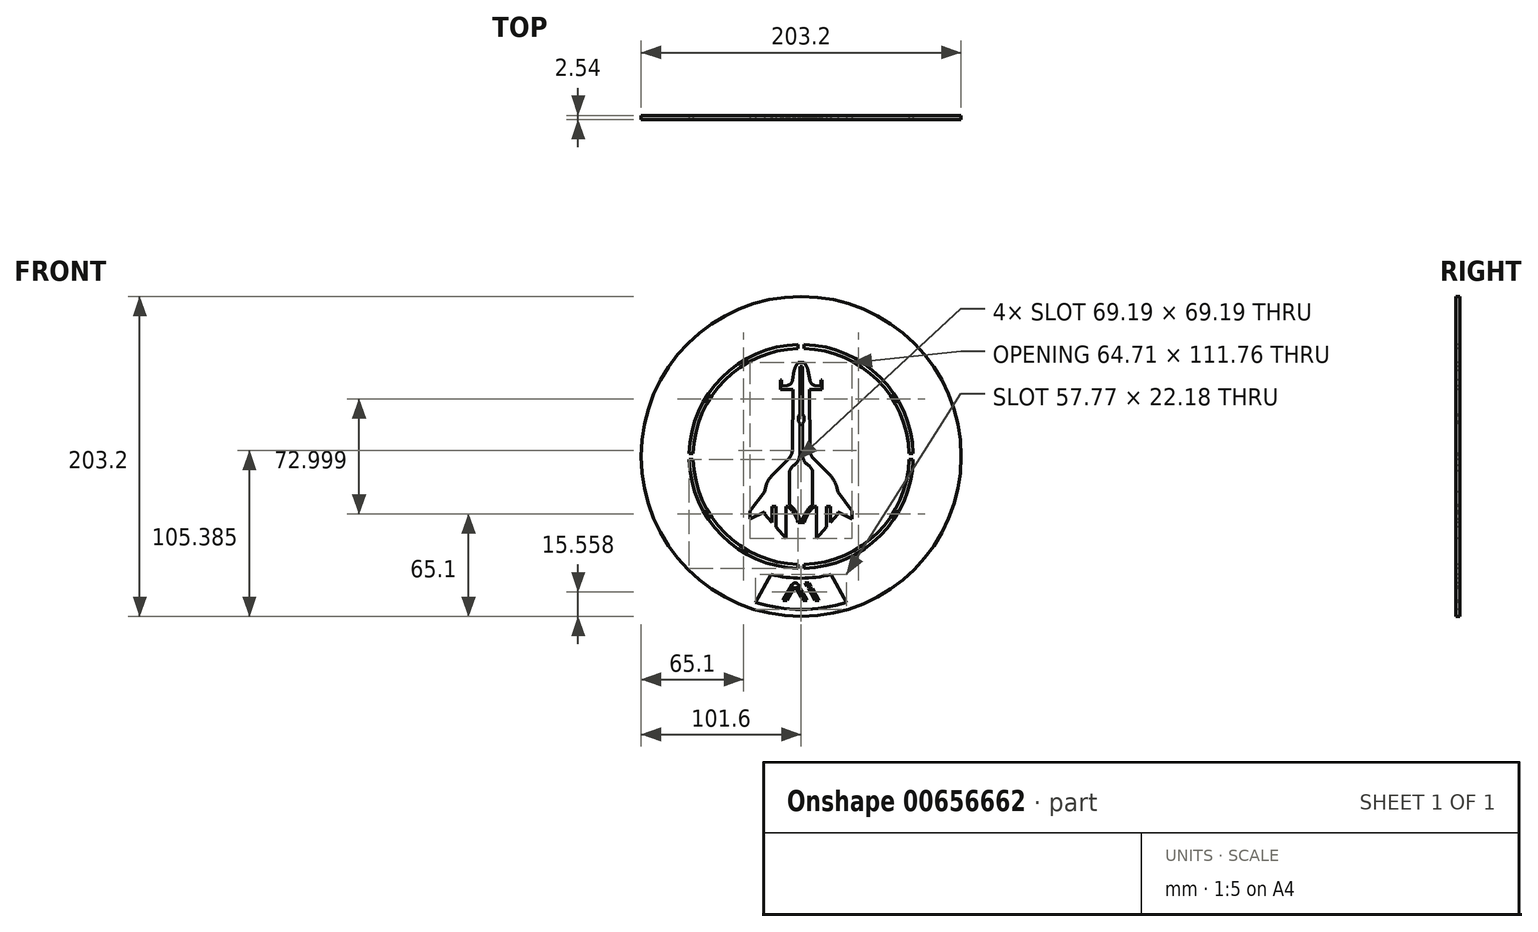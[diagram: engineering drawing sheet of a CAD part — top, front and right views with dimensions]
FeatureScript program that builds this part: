
annotation { "Feature Type Name" : "Feature", "Feature Type Description" : "" }
export const myFeature = defineFeature(function(context is Context, id is Id, definition is map)
    precondition{}
    {
        {
            var Q0;
            Q0=qCreatedBy(makeId("Front.planeOp"),FACE);
            var sketch = newSketch(context, id + "F0", { "sketchPlane" : qUnion([Q0])});
            skCircle(sketch, "E0", {"center": v(0, 0) * mm, "radius": 101.6 * mm});
            skSolve(sketch);
        }
        {
            var Q0;
            Q0=makeQuery(id+"F0.imprint","IMPRINT",FACE,{"disambiguationData":[TD([[makeQuery(id+"F0.imprint","IMPRINT",EDGE,{"derivedFrom":sQuery(id+"F0.wireOp",EDGE,"E0")}),1.0]])]});
            extrude(context, id + "F1", {"entities" : qUnion([Q0]), "oppositeDirection" : true, "depth" : 2.54 * mm, "offsetDistance" : 25.4 * mm});
        }
        {
            var Q0;
            Q0=makeQuery(id+"F1.opExtrude","CAP_FACE",FACE,{"disambiguationData":[OSD([sQuery(id+"F0.wireOp",EDGE,"E0")])],"isStart":true});
            var sketch = newSketch(context, id + "F2", { "sketchPlane" : qUnion([Q0])});
            skArc(sketch, "E1", {"start": v(-71.1, -1.9) * mm, "mid": v(-50.29, -50.29) * mm, "end": v(-1.9, -71.1) * mm});
            skArc(sketch, "E2", {"start": v(-68.55, -1.9) * mm, "mid": v(-48.5, -48.5) * mm, "end": v(-1.9, -68.55) * mm});
            skLineSegment(sketch, "E3", {"start": v(-68.55, 1.9) * mm, "end": v(-71.1, 1.9) * mm});
            skLineSegment(sketch, "E4", {"start": v(-68.55, -1.9) * mm, "end": v(-71.1, -1.9) * mm});
            skLineSegment(sketch, "E5.1.0", {"start": v(-1.9, 68.55) * mm, "end": v(-1.9, 71.1) * mm});
            skLineSegment(sketch, "E5.1.1", {"start": v(1.9, 68.55) * mm, "end": v(1.9, 71.1) * mm});
            skLineSegment(sketch, "E5.2.0", {"start": v(68.55, 1.9) * mm, "end": v(71.1, 1.9) * mm});
            skLineSegment(sketch, "E5.2.1", {"start": v(68.55, -1.9) * mm, "end": v(71.1, -1.9) * mm});
            skLineSegment(sketch, "E5.anchor1", {"start": v(0, 0) * mm, "end": v(-71.1, -1.9) * mm, "construction": true});
            skLineSegment(sketch, "E5.anchor2", {"start": v(0, 0) * mm, "end": v(71.1, 1.9) * mm, "construction": true});
            skLineSegment(sketch, "E6.1.0", {"start": v(1.9, -68.55) * mm, "end": v(1.9, -71.1) * mm});
            skLineSegment(sketch, "E6.1.1", {"start": v(-1.9, -68.55) * mm, "end": v(-1.9, -71.1) * mm});
            skLineSegment(sketch, "E6.anchor1", {"start": v(0, 0) * mm, "end": v(68.55, 1.9) * mm, "construction": true});
            skLineSegment(sketch, "E6.anchor2", {"start": v(0, 0) * mm, "end": v(-68.55, -1.9) * mm, "construction": true});
            skArc(sketch, "E7.trimOffspring", {"start": v(1.9, -68.55) * mm, "mid": v(48.5, -48.5) * mm, "end": v(68.55, -1.9) * mm});
            skArc(sketch, "E8.trimOffspring", {"start": v(1.9, -71.1) * mm, "mid": v(50.29, -50.29) * mm, "end": v(71.1, -1.9) * mm});
            skArc(sketch, "E9.trimOffspring", {"start": v(68.56, 1.84) * mm, "mid": v(48.52, 48.47) * mm, "end": v(1.9, 68.55) * mm});
            skArc(sketch, "E10.trimOffspring", {"start": v(71.1, 1.9) * mm, "mid": v(50.29, 50.29) * mm, "end": v(1.9, 71.1) * mm});
            skArc(sketch, "E11.trimOffspring", {"start": v(-1.9, 68.55) * mm, "mid": v(-48.5, 48.5) * mm, "end": v(-68.55, 1.9) * mm});
            skArc(sketch, "E12.trimOffspring", {"start": v(-1.9, 71.1) * mm, "mid": v(-50.29, 50.29) * mm, "end": v(-71.1, 1.9) * mm});
            skSolve(sketch);
        }
        {
            var Q0;
            Q0 = qSketchRegion(id + "F2", true);
            extrude(context, id + "F3", {"entities" : qUnion([Q0]), "operationType" : NewBodyOperationType.REMOVE, "oppositeDirection" : true, "depth" : 25.4 * mm, "offsetDistance" : 25.4 * mm});
        }
        {
            var Q0;
            Q0=makeQuery(id+"F1.opExtrude","CAP_FACE",FACE,{"disambiguationData":[OSD([sQuery(id+"F0.wireOp",EDGE,"E0")])],"isStart":true});
            var sketch = newSketch(context, id + "F4", { "sketchPlane" : qUnion([Q0])});
            skLineSegment(sketch, "E13", {"start": v(-1.9, 59.66) * mm, "end": v(1.9, 59.66) * mm});
            skArc(sketch, "E14", {"start": v(-1.9, 59.66) * mm, "mid": v(-3.46, 57.27) * mm, "end": v(-4.44, 54.58) * mm});
            skArc(sketch, "E15", {"start": v(4.44, 54.58) * mm, "mid": v(3.46, 57.27) * mm, "end": v(1.9, 59.66) * mm});
            skLineSegment(sketch, "E16", {"start": v(-4.44, 54.58) * mm, "end": v(-5.55, 48.33) * mm});
            skLineSegment(sketch, "E17", {"start": v(4.44, 54.58) * mm, "end": v(5.55, 48.33) * mm});
            skArc(sketch, "E18", {"start": v(-8.85, 45.17) * mm, "mid": v(-6.68, 46.2) * mm, "end": v(-5.55, 48.33) * mm});
            skLineSegment(sketch, "E19", {"start": v(-8.85, 45.17) * mm, "end": v(-12.63, 44.67) * mm});
            skLineSegment(sketch, "E20", {"start": v(-12.63, 44.67) * mm, "end": v(-12.63, 48.48) * mm});
            skLineSegment(sketch, "E21", {"start": v(-12.63, 48.48) * mm, "end": v(-13.13, 48.48) * mm});
            skLineSegment(sketch, "E22", {"start": v(-13.13, 48.48) * mm, "end": v(-13.13, 42.63) * mm});
            skLineSegment(sketch, "E23", {"start": v(-13.13, 42.63) * mm, "end": v(-5.25, 42.63) * mm});
            skLineSegment(sketch, "E24", {"start": v(-5.25, 42.63) * mm, "end": v(-5.59, 4.07) * mm});
            skArc(sketch, "E25", {"start": v(-7.76, -1.19) * mm, "mid": v(-6.16, 1.23) * mm, "end": v(-5.59, 4.07) * mm});
            skLineSegment(sketch, "E26", {"start": v(-7.76, -1.19) * mm, "end": v(-18.52, -12.21) * mm});
            skArc(sketch, "E27", {"start": v(-18.52, -12.21) * mm, "mid": v(-20.83, -15.27) * mm, "end": v(-22.31, -18.8) * mm});
            skLineSegment(sketch, "E28", {"start": v(-22.31, -18.8) * mm, "end": v(-23.32, -22.48) * mm});
            skLineSegment(sketch, "E29", {"start": v(-23.32, -22.48) * mm, "end": v(-32.35, -34.75) * mm});
            skLineSegment(sketch, "E30", {"start": v(-32.35, -34.75) * mm, "end": v(-32.35, -39.83) * mm});
            skLineSegment(sketch, "E31", {"start": v(-32.35, -39.83) * mm, "end": v(-23.32, -35.18) * mm});
            skLineSegment(sketch, "E32", {"start": v(-23.32, -35.18) * mm, "end": v(-23.32, -36.45) * mm});
            skLineSegment(sketch, "E33", {"start": v(-23.32, -36.45) * mm, "end": v(-18.52, -41.93) * mm});
            skLineSegment(sketch, "E34", {"start": v(-18.52, -41.93) * mm, "end": v(-18.52, -31.77) * mm});
            skLineSegment(sketch, "E35", {"start": v(-18.52, -31.77) * mm, "end": v(-15.98, -31.77) * mm});
            skLineSegment(sketch, "E36", {"start": v(-15.98, -31.77) * mm, "end": v(-15.98, -44.84) * mm});
            skLineSegment(sketch, "E37", {"start": v(-15.98, -44.84) * mm, "end": v(-9.63, -52.1) * mm});
            skLineSegment(sketch, "E38", {"start": v(-9.63, -52.1) * mm, "end": v(-9.63, -31.77) * mm});
            skLineSegment(sketch, "E39", {"start": v(-9.63, -31.77) * mm, "end": v(-8.36, -31.77) * mm});
            skLineSegment(sketch, "E40", {"start": v(0, 0) * mm, "end": v(0, -65.9) * mm});
            skArc(sketch, "E41", {"start": v(-2.03, -41.93) * mm, "mid": v(-4.38, -36.34) * mm, "end": v(-8.36, -31.77) * mm});
            skLineSegment(sketch, "E42", {"start": v(-2.03, -41.93) * mm, "end": v(0, -41.93) * mm});
            skLineSegment(sketch, "E43.MirrorCS", {"start": v(2.03, -41.93) * mm, "end": v(0, -41.93) * mm});
            skArc(sketch, "E44.MirrorCS", {"start": v(2.03, -41.93) * mm, "mid": v(4.38, -36.34) * mm, "end": v(8.36, -31.77) * mm});
            skLineSegment(sketch, "E45.MirrorCS", {"start": v(9.63, -52.1) * mm, "end": v(9.63, -31.77) * mm});
            skLineSegment(sketch, "E46.MirrorCS", {"start": v(9.63, -31.77) * mm, "end": v(8.36, -31.77) * mm});
            skLineSegment(sketch, "E47.MirrorCS", {"start": v(15.98, -44.84) * mm, "end": v(9.63, -52.1) * mm});
            skLineSegment(sketch, "E48.MirrorCS", {"start": v(15.98, -31.77) * mm, "end": v(15.98, -44.84) * mm});
            skLineSegment(sketch, "E49.MirrorCS", {"start": v(18.52, -31.77) * mm, "end": v(15.98, -31.77) * mm});
            skLineSegment(sketch, "E50.MirrorCS", {"start": v(18.52, -41.93) * mm, "end": v(18.52, -31.77) * mm});
            skLineSegment(sketch, "E51.MirrorCS", {"start": v(23.32, -36.45) * mm, "end": v(18.52, -41.93) * mm});
            skLineSegment(sketch, "E52.MirrorCS", {"start": v(23.32, -35.18) * mm, "end": v(23.32, -36.45) * mm});
            skLineSegment(sketch, "E53.MirrorCS", {"start": v(32.35, -39.83) * mm, "end": v(23.32, -35.18) * mm});
            skLineSegment(sketch, "E54.MirrorCS", {"start": v(32.35, -34.75) * mm, "end": v(32.35, -39.83) * mm});
            skLineSegment(sketch, "E55.MirrorCS", {"start": v(23.32, -22.48) * mm, "end": v(32.35, -34.75) * mm});
            skLineSegment(sketch, "E56.MirrorCS", {"start": v(22.31, -18.8) * mm, "end": v(23.32, -22.48) * mm});
            skArc(sketch, "E57.MirrorCS", {"start": v(18.52, -12.21) * mm, "mid": v(20.83, -15.27) * mm, "end": v(22.31, -18.8) * mm});
            skLineSegment(sketch, "E58.MirrorCS", {"start": v(7.76, -1.19) * mm, "end": v(18.52, -12.21) * mm});
            skArc(sketch, "E59.MirrorCS", {"start": v(7.76, -1.19) * mm, "mid": v(6.16, 1.23) * mm, "end": v(5.59, 4.07) * mm});
            skLineSegment(sketch, "E60.MirrorCS", {"start": v(5.25, 42.63) * mm, "end": v(5.59, 4.07) * mm});
            skLineSegment(sketch, "E61.MirrorCS", {"start": v(13.13, 42.63) * mm, "end": v(5.25, 42.63) * mm});
            skLineSegment(sketch, "E62.MirrorCS", {"start": v(13.13, 48.48) * mm, "end": v(13.13, 42.63) * mm});
            skLineSegment(sketch, "E63.MirrorCS", {"start": v(12.63, 48.48) * mm, "end": v(13.13, 48.48) * mm});
            skLineSegment(sketch, "E64.MirrorCS", {"start": v(12.63, 44.67) * mm, "end": v(12.63, 48.48) * mm});
            skLineSegment(sketch, "E65.MirrorCS", {"start": v(8.85, 45.17) * mm, "end": v(12.63, 44.67) * mm});
            skArc(sketch, "E66.MirrorCS", {"start": v(8.85, 45.17) * mm, "mid": v(6.68, 46.2) * mm, "end": v(5.55, 48.33) * mm});
            skLineSegment(sketch, "E67", {"start": v(-1.02, -39.9) * mm, "end": v(0, -39.9) * mm});
            skArc(sketch, "E68", {"start": v(-1.02, -39.9) * mm, "mid": v(-3.5, -34.86) * mm, "end": v(-7.35, -30.76) * mm});
            skArc(sketch, "E69", {"start": v(-4.8, -5.61) * mm, "mid": v(-2.02, -2.95) * mm, "end": v(-0.89, 0.74) * mm});
            skLineSegment(sketch, "E70", {"start": v(-0.89, 0.74) * mm, "end": v(-0.89, 21.06) * mm});
            skLineSegment(sketch, "E71", {"start": v(-0.89, 21.06) * mm, "end": v(-1.74, 22.07) * mm});
            skLineSegment(sketch, "E72", {"start": v(-1.74, 22.07) * mm, "end": v(-1.74, 25.63) * mm});
            skLineSegment(sketch, "E73", {"start": v(-1.74, 25.63) * mm, "end": v(-0.89, 26.64) * mm});
            skLineSegment(sketch, "E74", {"start": v(-0.89, 26.64) * mm, "end": v(-0.89, 57.12) * mm});
            skLineSegment(sketch, "E75", {"start": v(-0.89, 57.12) * mm, "end": v(0, 57.12) * mm});
            skLineSegment(sketch, "E76", {"start": v(0, 0) * mm, "end": v(0, 99.45) * mm});
            skArc(sketch, "E77", {"start": v(-4.8, -5.61) * mm, "mid": v(-6.25, -7.27) * mm, "end": v(-7.35, -9.17) * mm});
            skLineSegment(sketch, "E78", {"start": v(-7.35, -9.17) * mm, "end": v(-7.35, -30.76) * mm});
            skLineSegment(sketch, "E79.MirrorCS", {"start": v(1.02, -39.9) * mm, "end": v(0, -39.9) * mm});
            skArc(sketch, "E80.MirrorCS", {"start": v(1.02, -39.9) * mm, "mid": v(3.5, -34.86) * mm, "end": v(7.35, -30.76) * mm});
            skLineSegment(sketch, "E81.MirrorCS", {"start": v(7.35, -9.17) * mm, "end": v(7.35, -30.76) * mm});
            skArc(sketch, "E82.MirrorCS", {"start": v(4.8, -5.61) * mm, "mid": v(6.25, -7.27) * mm, "end": v(7.35, -9.17) * mm});
            skArc(sketch, "E83.MirrorCS", {"start": v(4.8, -5.61) * mm, "mid": v(2.02, -2.95) * mm, "end": v(0.89, 0.74) * mm});
            skLineSegment(sketch, "E84.MirrorCS", {"start": v(0.89, 0.74) * mm, "end": v(0.89, 21.06) * mm});
            skLineSegment(sketch, "E85.MirrorCS", {"start": v(0.89, 21.06) * mm, "end": v(1.74, 22.07) * mm});
            skLineSegment(sketch, "E86.MirrorCS", {"start": v(1.74, 22.07) * mm, "end": v(1.74, 25.63) * mm});
            skLineSegment(sketch, "E87.MirrorCS", {"start": v(1.74, 25.63) * mm, "end": v(0.89, 26.64) * mm});
            skLineSegment(sketch, "E88.MirrorCS", {"start": v(0.89, 26.64) * mm, "end": v(0.89, 57.12) * mm});
            skLineSegment(sketch, "E89.MirrorCS", {"start": v(0.89, 57.12) * mm, "end": v(0, 57.12) * mm});
            skSolve(sketch);
        }
        {
            var Q0;
            {var subQ0=sQuery(id+"F4.wireOp",EDGE,"E15");Q0=makeQuery(id+"F4.imprint","IMPRINT",FACE,{"disambiguationData":[TD([[makeQuery(id+"F4.imprint","IMPRINT",EDGE,{"derivedFrom":subQ0}),1.0]])]});}
            var Q1;
            {var subQ4=sQuery(id+"F4.wireOp",EDGE,"E14");Q1=makeQuery(id+"F4.imprint","IMPRINT",FACE,{"disambiguationData":[TD([[makeQuery(id+"F4.imprint","IMPRINT",EDGE,{"derivedFrom":subQ4}),1.0]])]});}
            extrude(context, id + "F5", {"entities" : qUnion([Q0, Q1]), "operationType" : NewBodyOperationType.REMOVE, "oppositeDirection" : true, "depth" : 25.4 * mm, "offsetDistance" : 25.4 * mm});
        }
        {
            var Q0;
            {var subQ0=sQuery(id+"F0.wireOp",EDGE,"E0");Q0=makeQuery(id+"F5.boolean.opBoolean","SPLIT",FACE,{"disambiguationData":[TD([makeQuery(id+"F1.opExtrude","SWEPT_FACE",FACE,{"disambiguationData":[OSD([subQ0])]})])],"derivedFrom":makeQuery(id+"F1.opExtrude","CAP_FACE",FACE,{"disambiguationData":[OSD([subQ0])],"isStart":true})});}
            var sketch = newSketch(context, id + "F6", { "sketchPlane" : qUnion([Q0])});
            skLineSegment(sketch, "E90", {"start": v(-28.89, -92.73) * mm, "end": v(-19.05, -74.95) * mm});
            skArc(sketch, "E91", {"start": v(-19.05, -74.95) * mm, "mid": v(0, -77.34) * mm, "end": v(19.05, -74.95) * mm});
            skLineSegment(sketch, "E92", {"start": v(19.05, -74.95) * mm, "end": v(28.89, -92.73) * mm});
            skArc(sketch, "E93", {"start": v(-28.89, -92.73) * mm, "mid": v(0, -97.13) * mm, "end": v(28.89, -92.73) * mm});
            skLineSegment(sketch, "E94", {"start": v(-8.89, -91.46) * mm, "end": v(-3.81, -82.57) * mm});
            skLineSegment(sketch, "E95", {"start": v(-3.81, -82.57) * mm, "end": v(1.27, -91.46) * mm});
            skLineSegment(sketch, "E96", {"start": v(-8.89, -91.46) * mm, "end": v(-11.43, -91.46) * mm});
            skLineSegment(sketch, "E97", {"start": v(-11.43, -91.46) * mm, "end": v(-5.72, -81.48) * mm});
            skLineSegment(sketch, "E98", {"start": v(1.27, -91.46) * mm, "end": v(3.81, -91.46) * mm});
            skLineSegment(sketch, "E99", {"start": v(3.81, -91.46) * mm, "end": v(-1.9, -81.48) * mm});
            skArc(sketch, "E100", {"start": v(-1.9, -81.48) * mm, "mid": v(-3.81, -80.37) * mm, "end": v(-5.72, -81.48) * mm});
            skLineSegment(sketch, "E101", {"start": v(8.9, -91.46) * mm, "end": v(4.54, -83.84) * mm});
            skLineSegment(sketch, "E102", {"start": v(4.54, -83.84) * mm, "end": v(7.08, -83.84) * mm});
            skLineSegment(sketch, "E103", {"start": v(7.08, -83.84) * mm, "end": v(11.43, -91.46) * mm});
            skLineSegment(sketch, "E104", {"start": v(11.43, -91.46) * mm, "end": v(8.9, -91.46) * mm});
            skLineSegment(sketch, "E105", {"start": v(3.8, -82.57) * mm, "end": v(6.35, -82.57) * mm});
            skLineSegment(sketch, "E106", {"start": v(6.35, -82.57) * mm, "end": v(5.09, -80.37) * mm});
            skLineSegment(sketch, "E107", {"start": v(5.09, -80.37) * mm, "end": v(2.55, -80.37) * mm});
            skLineSegment(sketch, "E108", {"start": v(2.55, -80.37) * mm, "end": v(3.8, -82.57) * mm});
            skSolve(sketch);
        }
        {
            var Q0;
            Q0=makeQuery(id+"F6.imprint","IMPRINT",FACE,{"disambiguationData":[TD([[makeQuery(id+"F6.imprint","IMPRINT",EDGE,{"derivedFrom":sQuery(id+"F6.wireOp",EDGE,"E90")}),-1.0]])]});
            extrude(context, id + "F7", {"entities" : qUnion([Q0]), "operationType" : NewBodyOperationType.REMOVE, "oppositeDirection" : true, "depth" : 25.4 * mm, "offsetDistance" : 25.4 * mm});
        }
    });
